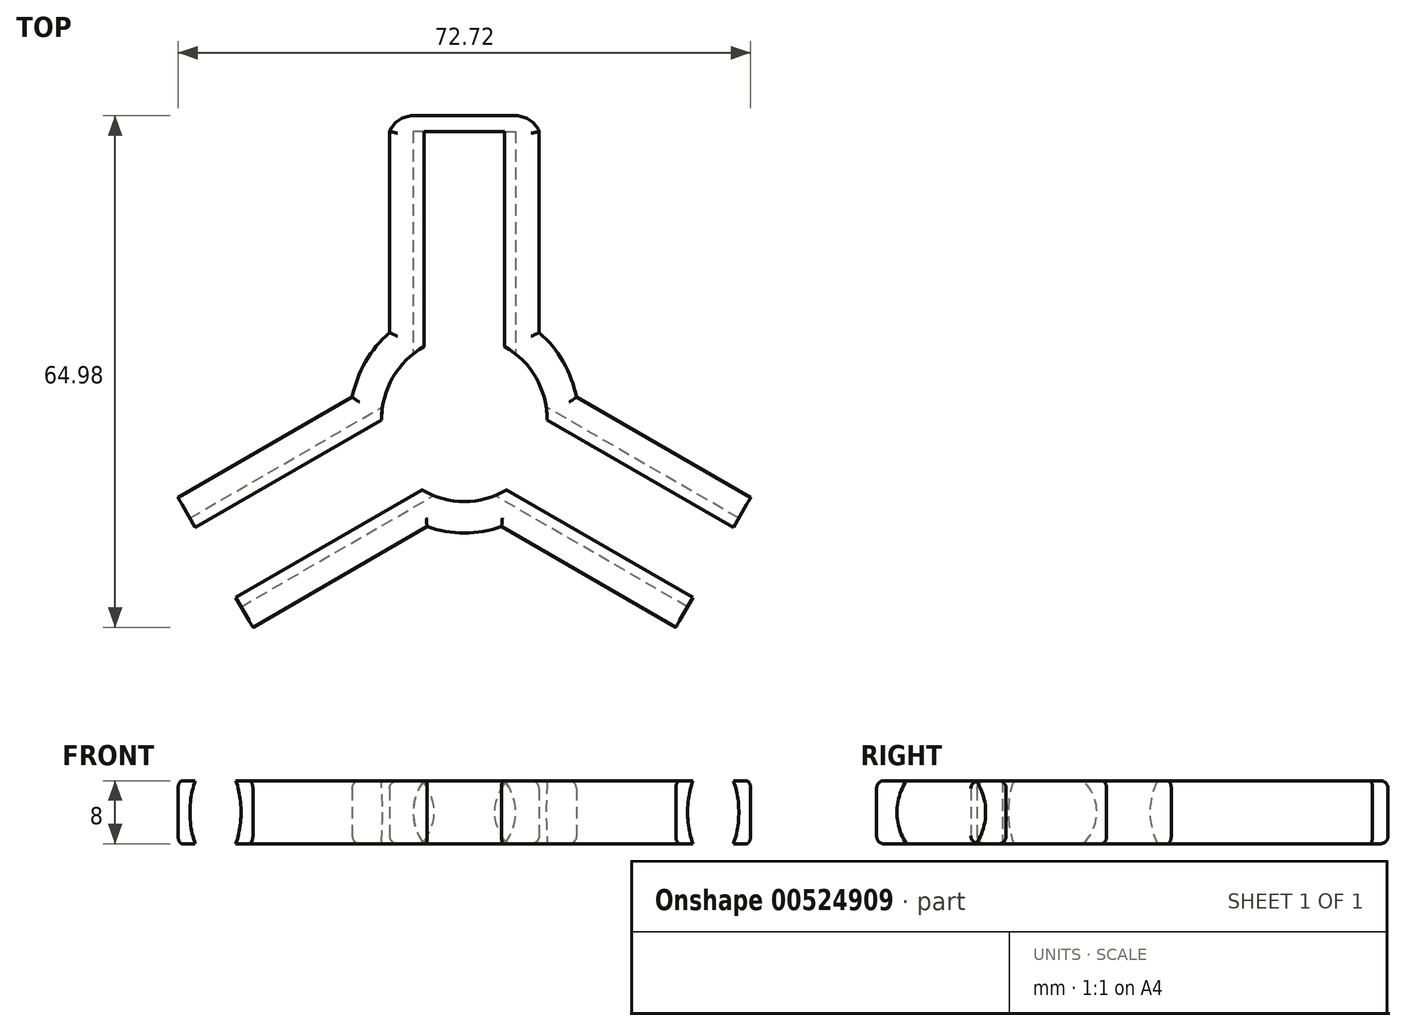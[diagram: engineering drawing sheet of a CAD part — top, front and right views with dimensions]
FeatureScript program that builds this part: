
annotation { "Feature Type Name" : "Feature", "Feature Type Description" : "" }
export const myFeature = defineFeature(function(context is Context, id is Id, definition is map)
    precondition{}
    {
        {
            var Q0;
            Q0=qCreatedBy(makeId("Top.planeOp"),FACE);
            var sketch = newSketch(context, id + "F0", { "sketchPlane" : qUnion([Q0])});
            skCircle(sketch, "E0", {"center": v(0, 0) * mm, "radius": 10.5 * mm});
            skCircle(sketch, "E1.0", {"center": v(0, 0) * mm, "radius": 14.5 * mm});
            skLineSegment(sketch, "E2", {"start": v(0, 36.5) * mm, "end": v(0, 10.5) * mm});
            skLineSegment(sketch, "E3", {"start": v(0, 36.5) * mm, "end": v(6.5, 36.5) * mm});
            skLineSegment(sketch, "E4.MirrorCS", {"start": v(0, 36.5) * mm, "end": v(-6.5, 36.5) * mm});
            skLineSegment(sketch, "E5.0", {"start": v(0, 38.5) * mm, "end": v(6.5, 38.5) * mm});
            skLineSegment(sketch, "E5.1", {"start": v(0, 38.5) * mm, "end": v(-6.5, 38.5) * mm});
            skLineSegment(sketch, "E6", {"start": v(-6.5, 36.5) * mm, "end": v(-6.5, 8.25) * mm});
            skLineSegment(sketch, "E7.0", {"start": v(-9.5, 36.5) * mm, "end": v(-9.5, 10.95) * mm});
            skArc(sketch, "E8", {"start": v(-6.5, 38.5) * mm, "mid": v(-8.3, 37.95) * mm, "end": v(-9.5, 36.5) * mm});
            skLineSegment(sketch, "E9.MirrorCS", {"start": v(6.5, 36.5) * mm, "end": v(6.5, 8.25) * mm});
            skLineSegment(sketch, "E10.MirrorCS", {"start": v(9.5, 36.5) * mm, "end": v(9.5, 10.95) * mm});
            skArc(sketch, "E11.MirrorCS", {"start": v(6.5, 38.5) * mm, "mid": v(8.3, 37.95) * mm, "end": v(9.5, 36.5) * mm});
            skPoint(sketch, "E12.orphan", {"position": v(9.5, 8.25) * mm});
            skPoint(sketch, "E13.orphan", {"position": v(-9.5, 8.25) * mm});
            skLineSegment(sketch, "E14.1.0", {"start": v(-34.86, -12.62) * mm, "end": v(-10.4, 1.5) * mm});
            skLineSegment(sketch, "E14.1.1", {"start": v(-36.36, -10.02) * mm, "end": v(-14.24, 2.75) * mm});
            skArc(sketch, "E14.1.2", {"start": v(-36.6, -13.62) * mm, "mid": v(-37.02, -11.79) * mm, "end": v(-36.36, -10.02) * mm});
            skLineSegment(sketch, "E14.1.3", {"start": v(-33.34, -19.25) * mm, "end": v(-36.6, -13.62) * mm});
            skLineSegment(sketch, "E14.1.4", {"start": v(-31.6, -18.25) * mm, "end": v(-34.86, -12.62) * mm});
            skLineSegment(sketch, "E14.1.5", {"start": v(-31.6, -18.25) * mm, "end": v(-28.36, -23.88) * mm});
            skLineSegment(sketch, "E14.1.6", {"start": v(-33.34, -19.25) * mm, "end": v(-30.1, -24.88) * mm});
            skLineSegment(sketch, "E14.1.7", {"start": v(-31.6, -18.25) * mm, "end": v(-9.1, -5.25) * mm});
            skLineSegment(sketch, "E14.1.8", {"start": v(-28.36, -23.88) * mm, "end": v(-3.9, -9.75) * mm});
            skLineSegment(sketch, "E14.1.9", {"start": v(-26.86, -26.48) * mm, "end": v(-4.74, -13.7) * mm});
            skArc(sketch, "E14.1.10", {"start": v(-30.1, -24.88) * mm, "mid": v(-28.72, -26.17) * mm, "end": v(-26.86, -26.48) * mm});
            skLineSegment(sketch, "E14.2.0", {"start": v(28.36, -23.88) * mm, "end": v(3.9, -9.75) * mm});
            skLineSegment(sketch, "E14.2.1", {"start": v(26.86, -26.48) * mm, "end": v(4.74, -13.7) * mm});
            skArc(sketch, "E14.2.2", {"start": v(30.1, -24.88) * mm, "mid": v(28.72, -26.17) * mm, "end": v(26.86, -26.48) * mm});
            skLineSegment(sketch, "E14.2.3", {"start": v(33.34, -19.25) * mm, "end": v(30.1, -24.88) * mm});
            skLineSegment(sketch, "E14.2.4", {"start": v(31.6, -18.25) * mm, "end": v(28.36, -23.88) * mm});
            skLineSegment(sketch, "E14.2.5", {"start": v(31.6, -18.25) * mm, "end": v(34.86, -12.62) * mm});
            skLineSegment(sketch, "E14.2.6", {"start": v(33.34, -19.25) * mm, "end": v(36.6, -13.62) * mm});
            skLineSegment(sketch, "E14.2.7", {"start": v(31.6, -18.25) * mm, "end": v(9.1, -5.25) * mm});
            skLineSegment(sketch, "E14.2.8", {"start": v(34.86, -12.62) * mm, "end": v(10.4, 1.5) * mm});
            skLineSegment(sketch, "E14.2.9", {"start": v(36.36, -10.02) * mm, "end": v(14.24, 2.75) * mm});
            skArc(sketch, "E14.2.10", {"start": v(36.6, -13.62) * mm, "mid": v(37.02, -11.79) * mm, "end": v(36.36, -10.02) * mm});
            skLineSegment(sketch, "E15", {"start": v(0, 10.5) * mm, "end": v(0, 5.05) * mm});
            skLineSegment(sketch, "E16.1.0", {"start": v(-9.1, -5.25) * mm, "end": v(-4.37, -2.52) * mm});
            skLineSegment(sketch, "E16.2.0", {"start": v(9.1, -5.25) * mm, "end": v(4.37, -2.52) * mm});
            skLineSegment(sketch, "E17", {"start": v(6.5, 36.5) * mm, "end": v(13.9, 36.5) * mm});
            skLineSegment(sketch, "E18", {"start": v(-6.5, 36.5) * mm, "end": v(-15.3, 36.5) * mm});
            skLineSegment(sketch, "E19.1.0", {"start": v(-28.36, -23.88) * mm, "end": v(-23.96, -31.5) * mm});
            skLineSegment(sketch, "E19.1.1", {"start": v(-34.86, -12.62) * mm, "end": v(-38.56, -6.21) * mm});
            skLineSegment(sketch, "E19.2.0", {"start": v(34.86, -12.62) * mm, "end": v(39.26, -5) * mm});
            skLineSegment(sketch, "E19.2.1", {"start": v(28.36, -23.88) * mm, "end": v(24.66, -30.29) * mm});
            skSolve(sketch);
        }
        {
            var Q0;
            {var subQ0=sQuery(id+"F0.wireOp",EDGE,"E7.0");Q0=makeQuery(id+"F0.imprint","IMPRINT",FACE,{"disambiguationData":[TD([[makeQuery(id+"F0.imprint","IMPRINT",EDGE,{"derivedFrom":subQ0}),1.0]])]});}
            var Q1;
            {var subQ0=sQuery(id+"F0.wireOp",EDGE,"E10.MirrorCS");Q1=makeQuery(id+"F0.imprint","IMPRINT",FACE,{"disambiguationData":[TD([[makeQuery(id+"F0.imprint","IMPRINT",EDGE,{"derivedFrom":subQ0}),-1.0]])]});}
            var Q2;
            {var subQ0=sQuery(id+"F0.wireOp",EDGE,"E2");var subQ1=sQuery(id+"F0.wireOp",EDGE,"E0");var subQ2=makeQuery(id+"F0.imprint","INTERSECT",VERTEX,{"derivedFrom":[subQ1,subQ0]});Q2=makeQuery(id+"F0.imprint","IMPRINT",FACE,{"disambiguationData":[TD([[makeQuery(id+"F0.imprint","IMPRINT",EDGE,{"disambiguationData":[TD([[subQ2,1.0]])],"derivedFrom":subQ1}),-1.0]])]});}
            var Q3;
            {var subQ5=sQuery(id+"F0.wireOp",EDGE,"E9.MirrorCS");var subQ7=sQuery(id+"F0.wireOp",EDGE,"E0");var subQ8=makeQuery(id+"F0.imprint","INTERSECT",VERTEX,{"derivedFrom":[subQ7,subQ5]});Q3=makeQuery(id+"F0.imprint","IMPRINT",FACE,{"disambiguationData":[TD([[makeQuery(id+"F0.imprint","IMPRINT",EDGE,{"disambiguationData":[TD([[subQ8,1.0]])],"derivedFrom":subQ7}),-1.0]])]});}
            var Q4;
            {var subQ0=sQuery(id+"F0.wireOp",EDGE,"E2");var subQ1=sQuery(id+"F0.wireOp",EDGE,"E0");var subQ2=makeQuery(id+"F0.imprint","INTERSECT",VERTEX,{"derivedFrom":[subQ1,subQ0]});Q4=makeQuery(id+"F0.imprint","IMPRINT",FACE,{"disambiguationData":[TD([[makeQuery(id+"F0.imprint","IMPRINT",EDGE,{"disambiguationData":[TD([[subQ2,-1.0]])],"derivedFrom":subQ1}),-1.0]])]});}
            var Q5;
            {var subQ5=sQuery(id+"F0.wireOp",EDGE,"E6");var subQ6=sQuery(id+"F0.wireOp",EDGE,"E0");var subQ7=makeQuery(id+"F0.imprint","INTERSECT",VERTEX,{"derivedFrom":[subQ6,subQ5]});Q5=makeQuery(id+"F0.imprint","IMPRINT",FACE,{"disambiguationData":[TD([[makeQuery(id+"F0.imprint","IMPRINT",EDGE,{"disambiguationData":[TD([[subQ7,-1.0]])],"derivedFrom":subQ6}),-1.0]])]});}
            var Q6;
            {var subQ0=sQuery(id+"F0.wireOp",EDGE,"E14.1.1");Q6=makeQuery(id+"F0.imprint","IMPRINT",FACE,{"disambiguationData":[TD([[makeQuery(id+"F0.imprint","IMPRINT",EDGE,{"derivedFrom":subQ0}),-1.0]])]});}
            var Q7;
            {var subQ0=sQuery(id+"F0.wireOp",EDGE,"E14.1.0");var subQ1=sQuery(id+"F0.wireOp",EDGE,"E0");var subQ2=makeQuery(id+"F0.imprint","INTERSECT",VERTEX,{"derivedFrom":[subQ1,subQ0]});Q7=makeQuery(id+"F0.imprint","IMPRINT",FACE,{"disambiguationData":[TD([[makeQuery(id+"F0.imprint","IMPRINT",EDGE,{"disambiguationData":[TD([[subQ2,-1.0]])],"derivedFrom":subQ1}),-1.0]])]});}
            var Q8;
            {var subQ0=sQuery(id+"F0.wireOp",EDGE,"E14.1.7");var subQ1=sQuery(id+"F0.wireOp",EDGE,"E0");var subQ2=makeQuery(id+"F0.imprint","INTERSECT",VERTEX,{"derivedFrom":[subQ1,subQ0]});Q8=makeQuery(id+"F0.imprint","IMPRINT",FACE,{"disambiguationData":[TD([[makeQuery(id+"F0.imprint","IMPRINT",EDGE,{"disambiguationData":[TD([[subQ2,-1.0]])],"derivedFrom":subQ1}),-1.0]])]});}
            var Q9;
            {var subQ0=sQuery(id+"F0.wireOp",EDGE,"E14.1.9");Q9=makeQuery(id+"F0.imprint","IMPRINT",FACE,{"disambiguationData":[TD([[makeQuery(id+"F0.imprint","IMPRINT",EDGE,{"derivedFrom":subQ0}),1.0]])]});}
            var Q10;
            {var subQ4=sQuery(id+"F0.wireOp",EDGE,"E0");var subQ7=sQuery(id+"F0.wireOp",EDGE,"E14.1.8");var subQ9=makeQuery(id+"F0.imprint","INTERSECT",VERTEX,{"derivedFrom":[subQ4,subQ7]});Q10=makeQuery(id+"F0.imprint","IMPRINT",FACE,{"disambiguationData":[TD([[makeQuery(id+"F0.imprint","IMPRINT",EDGE,{"disambiguationData":[TD([[subQ9,-1.0]])],"derivedFrom":subQ4}),-1.0]])]});}
            var Q11;
            {var subQ0=sQuery(id+"F0.wireOp",EDGE,"E14.2.1");Q11=makeQuery(id+"F0.imprint","IMPRINT",FACE,{"disambiguationData":[TD([[makeQuery(id+"F0.imprint","IMPRINT",EDGE,{"derivedFrom":subQ0}),-1.0]])]});}
            var Q12;
            {var subQ0=sQuery(id+"F0.wireOp",EDGE,"E14.2.0");var subQ1=sQuery(id+"F0.wireOp",EDGE,"E0");var subQ2=makeQuery(id+"F0.imprint","INTERSECT",VERTEX,{"derivedFrom":[subQ1,subQ0]});Q12=makeQuery(id+"F0.imprint","IMPRINT",FACE,{"disambiguationData":[TD([[makeQuery(id+"F0.imprint","IMPRINT",EDGE,{"disambiguationData":[TD([[subQ2,-1.0]])],"derivedFrom":subQ1}),-1.0]])]});}
            var Q13;
            {var subQ0=sQuery(id+"F0.wireOp",EDGE,"E14.2.7");var subQ1=sQuery(id+"F0.wireOp",EDGE,"E0");var subQ2=makeQuery(id+"F0.imprint","INTERSECT",VERTEX,{"derivedFrom":[subQ1,subQ0]});Q13=makeQuery(id+"F0.imprint","IMPRINT",FACE,{"disambiguationData":[TD([[makeQuery(id+"F0.imprint","IMPRINT",EDGE,{"disambiguationData":[TD([[subQ2,-1.0]])],"derivedFrom":subQ1}),-1.0]])]});}
            var Q14;
            {var subQ0=sQuery(id+"F0.wireOp",EDGE,"E14.2.9");Q14=makeQuery(id+"F0.imprint","IMPRINT",FACE,{"disambiguationData":[TD([[makeQuery(id+"F0.imprint","IMPRINT",EDGE,{"derivedFrom":subQ0}),1.0]])]});}
            var Q15;
            {var subQ5=sQuery(id+"F0.wireOp",EDGE,"E3");Q15=makeQuery(id+"F0.imprint","IMPRINT",FACE,{"disambiguationData":[TD([[makeQuery(id+"F0.imprint","IMPRINT",EDGE,{"derivedFrom":subQ5}),-1.0]])]});}
            var Q16;
            {var subQ5=sQuery(id+"F0.wireOp",EDGE,"E4.MirrorCS");Q16=makeQuery(id+"F0.imprint","IMPRINT",FACE,{"disambiguationData":[TD([[makeQuery(id+"F0.imprint","IMPRINT",EDGE,{"derivedFrom":subQ5}),1.0]])]});}
            var Q17;
            {var subQ5=sQuery(id+"F0.wireOp",EDGE,"E14.1.4");Q17=makeQuery(id+"F0.imprint","IMPRINT",FACE,{"disambiguationData":[TD([[makeQuery(id+"F0.imprint","IMPRINT",EDGE,{"derivedFrom":subQ5}),-1.0]])]});}
            var Q18;
            {var subQ5=sQuery(id+"F0.wireOp",EDGE,"E14.1.5");Q18=makeQuery(id+"F0.imprint","IMPRINT",FACE,{"disambiguationData":[TD([[makeQuery(id+"F0.imprint","IMPRINT",EDGE,{"derivedFrom":subQ5}),1.0]])]});}
            var Q19;
            {var subQ5=sQuery(id+"F0.wireOp",EDGE,"E14.2.4");Q19=makeQuery(id+"F0.imprint","IMPRINT",FACE,{"disambiguationData":[TD([[makeQuery(id+"F0.imprint","IMPRINT",EDGE,{"derivedFrom":subQ5}),-1.0]])]});}
            var Q20;
            {var subQ5=sQuery(id+"F0.wireOp",EDGE,"E14.2.5");Q20=makeQuery(id+"F0.imprint","IMPRINT",FACE,{"disambiguationData":[TD([[makeQuery(id+"F0.imprint","IMPRINT",EDGE,{"derivedFrom":subQ5}),1.0]])]});}
            extrude(context, id + "F1", {"entities" : qUnion([Q0, Q1, Q2, Q3, Q4, Q5, Q6, Q7, Q8, Q9, Q10, Q11, Q12, Q13, Q14, Q15, Q16, Q17, Q18, Q19, Q20]), "endBound" : BoundingType.SYMMETRIC, "depth" : 8 * mm, "offsetDistance" : 25 * mm});
        }
        {
            var Q0;
            Q0=makeQuery(id+"F1.opExtrude","SWEPT_FACE",FACE,{"disambiguationData":[OSD([sQuery(id+"F0.wireOp",EDGE,"E18")])]});
            cPlane(context, id + "F2", {"entities" : qUnion([Q0]), "cplaneType" : CPlaneType.OFFSET, "offset" : 0 * mm, "width" : 150 * mm, "height" : 150 * mm});
        }
        {
            var Q0;
            Q0=qCreatedBy(id+"F2.planeOp",FACE);
            var sketch = newSketch(context, id + "F3", { "sketchPlane" : qUnion([Q0])});
            skCircle(sketch, "E20", {"center": v(0, 0) * mm, "radius": 6.5 * mm});
            skSolve(sketch);
        }
        {
            var Q0;
            Q0=makeQuery(id+"F3.imprint","IMPRINT",FACE,{"disambiguationData":[TD([[makeQuery(id+"F3.imprint","IMPRINT",EDGE,{"derivedFrom":sQuery(id+"F3.wireOp",EDGE,"E20")}),1.0]])]});
            var Q1;
            Q1=sQuery(id+"F0.wireOp",EDGE,"E2");
            var Q2;
            Q2=sQuery(id+"F0.wireOp",EDGE,"E15");
            sweep(context, id + "F4", {"operationType" : NewBodyOperationType.REMOVE, "profiles" : qUnion([Q0]), "path" : qUnion([Q1, Q2])});
        }
        {
            var Q0;
            Q0=makeQuery(id+"F1.opExtrude","SWEPT_FACE",FACE,{"disambiguationData":[OSD([sQuery(id+"F0.wireOp",EDGE,"E14.1.4"),sQuery(id+"F0.wireOp",EDGE,"E14.1.5"),sQuery(id+"F0.wireOp",EDGE,"E19.1.0"),sQuery(id+"F0.wireOp",EDGE,"E19.1.1")])]});
            cPlane(context, id + "F5", {"entities" : qUnion([Q0]), "cplaneType" : CPlaneType.OFFSET, "offset" : 0 * mm, "width" : 150 * mm, "height" : 150 * mm});
        }
        {
            var Q0;
            Q0=qCreatedBy(id+"F5.planeOp",FACE);
            var sketch = newSketch(context, id + "F6", { "sketchPlane" : qUnion([Q0])});
            skCircle(sketch, "E21", {"center": v(0, 0) * mm, "radius": 6.5 * mm});
            skSolve(sketch);
        }
        {
            var Q0;
            Q0=makeQuery(id+"F6.imprint","IMPRINT",FACE,{"disambiguationData":[TD([[makeQuery(id+"F6.imprint","IMPRINT",EDGE,{"derivedFrom":sQuery(id+"F6.wireOp",EDGE,"E21")}),1.0]])]});
            var Q1;
            Q1=sQuery(id+"F0.wireOp",EDGE,"E14.1.7");
            var Q2;
            Q2=sQuery(id+"F0.wireOp",EDGE,"E16.1.0");
            sweep(context, id + "F7", {"operationType" : NewBodyOperationType.REMOVE, "profiles" : qUnion([Q0]), "path" : qUnion([Q1, Q2])});
        }
        {
            var Q0;
            Q0=makeQuery(id+"F1.opExtrude","SWEPT_FACE",FACE,{"disambiguationData":[OSD([sQuery(id+"F0.wireOp",EDGE,"E14.2.4"),sQuery(id+"F0.wireOp",EDGE,"E14.2.5"),sQuery(id+"F0.wireOp",EDGE,"E19.2.0"),sQuery(id+"F0.wireOp",EDGE,"E19.2.1")])]});
            cPlane(context, id + "F8", {"entities" : qUnion([Q0]), "cplaneType" : CPlaneType.OFFSET, "offset" : 0 * mm, "width" : 150 * mm, "height" : 150 * mm});
        }
        {
            var Q0;
            Q0=qCreatedBy(id+"F8.planeOp",FACE);
            var sketch = newSketch(context, id + "F9", { "sketchPlane" : qUnion([Q0])});
            skCircle(sketch, "E22", {"center": v(0, 0) * mm, "radius": 6.5 * mm});
            skSolve(sketch);
        }
        {
            var Q0;
            Q0=makeQuery(id+"F9.imprint","IMPRINT",FACE,{"disambiguationData":[TD([[makeQuery(id+"F9.imprint","IMPRINT",EDGE,{"derivedFrom":sQuery(id+"F9.wireOp",EDGE,"E22")}),1.0]])]});
            var Q1;
            Q1=sQuery(id+"F0.wireOp",EDGE,"E14.2.7");
            var Q2;
            Q2=sQuery(id+"F0.wireOp",EDGE,"E16.2.0");
            sweep(context, id + "F10", {"operationType" : NewBodyOperationType.REMOVE, "profiles" : qUnion([Q0]), "path" : qUnion([Q1, Q2])});
        }
        {
            var Q0;
            {var subQ1=sQuery(id+"F0.wireOp",EDGE,"E3");Q0=makeQuery(id+"F0.imprint","IMPRINT",FACE,{"disambiguationData":[TD([[makeQuery(id+"F0.imprint","IMPRINT",EDGE,{"derivedFrom":subQ1}),1.0]])]});}
            var Q1;
            {var subQ2=sQuery(id+"F0.wireOp",EDGE,"E14.1.2");Q1=makeQuery(id+"F0.imprint","IMPRINT",FACE,{"disambiguationData":[TD([[makeQuery(id+"F0.imprint","IMPRINT",EDGE,{"derivedFrom":subQ2}),-1.0]])]});}
            var Q2;
            {var subQ2=sQuery(id+"F0.wireOp",EDGE,"E14.2.2");Q2=makeQuery(id+"F0.imprint","IMPRINT",FACE,{"disambiguationData":[TD([[makeQuery(id+"F0.imprint","IMPRINT",EDGE,{"derivedFrom":subQ2}),-1.0]])]});}
            extrude(context, id + "F11", {"entities" : qUnion([Q0, Q1, Q2]), "operationType" : NewBodyOperationType.ADD, "endBound" : BoundingType.SYMMETRIC, "depth" : 8 * mm, "offsetDistance" : 25 * mm});
        }
        {
            var Q0;
            Q0=makeQuery(id+"F1.opExtrude","CAP_EDGE",EDGE,{"disambiguationData":[OSD([sQuery(id+"F0.wireOp",EDGE,"E7.0")])],"isStart":true});
            var Q1;
            Q1=makeQuery(id+"F1.opExtrude","CAP_EDGE",EDGE,{"disambiguationData":[OSD([sQuery(id+"F0.wireOp",EDGE,"E10.MirrorCS")])],"isStart":true});
            var Q2;
            Q2=makeQuery(id+"F11.opExtrude","CAP_EDGE",EDGE,{"disambiguationData":[OSD([sQuery(id+"F0.wireOp",EDGE,"E5.0"),sQuery(id+"F0.wireOp",EDGE,"E5.1")])],"isStart":true});
            var Q3;
            {var subQ0=sQuery(id+"F0.wireOp",EDGE,"E1.0");Q3=makeQuery(id+"F1.opExtrude","CAP_EDGE",EDGE,{"disambiguationData":[OSD([subQ0]),TDD([makeQuery(id+"F0.imprint","IMPRINT",EDGE,{"disambiguationData":[TD([[makeQuery(id+"F0.imprint","INTERSECT",VERTEX,{"derivedFrom":[subQ0,sQuery(id+"F0.wireOp",EDGE,"E7.0")]}),-1.0]])],"derivedFrom":subQ0})])],"isStart":true});}
            var Q4;
            Q4=makeQuery(id+"F1.opExtrude","CAP_EDGE",EDGE,{"disambiguationData":[OSD([sQuery(id+"F0.wireOp",EDGE,"E14.1.1")])],"isStart":true});
            var Q5;
            Q5=makeQuery(id+"F11.opExtrude","CAP_EDGE",EDGE,{"disambiguationData":[OSD([sQuery(id+"F0.wireOp",EDGE,"E14.1.3"),sQuery(id+"F0.wireOp",EDGE,"E14.1.6")])],"isStart":true});
            var Q6;
            Q6=makeQuery(id+"F1.opExtrude","CAP_EDGE",EDGE,{"disambiguationData":[OSD([sQuery(id+"F0.wireOp",EDGE,"E14.1.9")])],"isStart":true});
            var Q7;
            {var subQ0=sQuery(id+"F0.wireOp",EDGE,"E1.0");Q7=makeQuery(id+"F1.opExtrude","CAP_EDGE",EDGE,{"disambiguationData":[OSD([subQ0]),TDD([makeQuery(id+"F0.imprint","IMPRINT",EDGE,{"disambiguationData":[TD([[makeQuery(id+"F0.imprint","INTERSECT",VERTEX,{"derivedFrom":[subQ0,sQuery(id+"F0.wireOp",EDGE,"E14.1.9")]}),-1.0]])],"derivedFrom":subQ0})])],"isStart":true});}
            var Q8;
            Q8=makeQuery(id+"F1.opExtrude","CAP_EDGE",EDGE,{"disambiguationData":[OSD([sQuery(id+"F0.wireOp",EDGE,"E14.2.1")])],"isStart":true});
            var Q9;
            Q9=makeQuery(id+"F11.opExtrude","CAP_EDGE",EDGE,{"disambiguationData":[OSD([sQuery(id+"F0.wireOp",EDGE,"E14.2.3"),sQuery(id+"F0.wireOp",EDGE,"E14.2.6")])],"isStart":true});
            var Q10;
            Q10=makeQuery(id+"F1.opExtrude","CAP_EDGE",EDGE,{"disambiguationData":[OSD([sQuery(id+"F0.wireOp",EDGE,"E14.2.9")])],"isStart":true});
            var Q11;
            {var subQ0=sQuery(id+"F0.wireOp",EDGE,"E1.0");Q11=makeQuery(id+"F1.opExtrude","CAP_EDGE",EDGE,{"disambiguationData":[OSD([subQ0]),TDD([makeQuery(id+"F0.imprint","IMPRINT",EDGE,{"disambiguationData":[TD([[makeQuery(id+"F0.imprint","INTERSECT",VERTEX,{"derivedFrom":[subQ0,sQuery(id+"F0.wireOp",EDGE,"E10.MirrorCS")]}),1.0]])],"derivedFrom":subQ0})])],"isStart":true});}
            var Q12;
            Q12=makeQuery(id+"F11.opExtrude","CAP_EDGE",EDGE,{"disambiguationData":[OSD([sQuery(id+"F0.wireOp",EDGE,"E5.0"),sQuery(id+"F0.wireOp",EDGE,"E5.1")])],"isStart":false});
            var Q13;
            Q13=makeQuery(id+"F1.opExtrude","CAP_EDGE",EDGE,{"disambiguationData":[OSD([sQuery(id+"F0.wireOp",EDGE,"E10.MirrorCS")])],"isStart":false});
            var Q14;
            {var subQ0=sQuery(id+"F0.wireOp",EDGE,"E1.0");Q14=makeQuery(id+"F1.opExtrude","CAP_EDGE",EDGE,{"disambiguationData":[OSD([subQ0]),TDD([makeQuery(id+"F0.imprint","IMPRINT",EDGE,{"disambiguationData":[TD([[makeQuery(id+"F0.imprint","INTERSECT",VERTEX,{"derivedFrom":[subQ0,sQuery(id+"F0.wireOp",EDGE,"E10.MirrorCS")]}),1.0]])],"derivedFrom":subQ0})])],"isStart":false});}
            var Q15;
            Q15=makeQuery(id+"F1.opExtrude","CAP_EDGE",EDGE,{"disambiguationData":[OSD([sQuery(id+"F0.wireOp",EDGE,"E14.2.9")])],"isStart":false});
            var Q16;
            Q16=makeQuery(id+"F11.opExtrude","CAP_EDGE",EDGE,{"disambiguationData":[OSD([sQuery(id+"F0.wireOp",EDGE,"E14.2.3"),sQuery(id+"F0.wireOp",EDGE,"E14.2.6")])],"isStart":false});
            var Q17;
            Q17=makeQuery(id+"F1.opExtrude","CAP_EDGE",EDGE,{"disambiguationData":[OSD([sQuery(id+"F0.wireOp",EDGE,"E14.2.1")])],"isStart":false});
            var Q18;
            {var subQ0=sQuery(id+"F0.wireOp",EDGE,"E1.0");Q18=makeQuery(id+"F1.opExtrude","CAP_EDGE",EDGE,{"disambiguationData":[OSD([subQ0]),TDD([makeQuery(id+"F0.imprint","IMPRINT",EDGE,{"disambiguationData":[TD([[makeQuery(id+"F0.imprint","INTERSECT",VERTEX,{"derivedFrom":[subQ0,sQuery(id+"F0.wireOp",EDGE,"E14.1.9")]}),-1.0]])],"derivedFrom":subQ0})])],"isStart":false});}
            var Q19;
            Q19=makeQuery(id+"F1.opExtrude","CAP_EDGE",EDGE,{"disambiguationData":[OSD([sQuery(id+"F0.wireOp",EDGE,"E14.1.9")])],"isStart":false});
            var Q20;
            Q20=makeQuery(id+"F11.opExtrude","CAP_EDGE",EDGE,{"disambiguationData":[OSD([sQuery(id+"F0.wireOp",EDGE,"E14.1.3"),sQuery(id+"F0.wireOp",EDGE,"E14.1.6")])],"isStart":false});
            var Q21;
            Q21=makeQuery(id+"F1.opExtrude","CAP_EDGE",EDGE,{"disambiguationData":[OSD([sQuery(id+"F0.wireOp",EDGE,"E14.1.1")])],"isStart":false});
            var Q22;
            {var subQ0=sQuery(id+"F0.wireOp",EDGE,"E1.0");Q22=makeQuery(id+"F1.opExtrude","CAP_EDGE",EDGE,{"disambiguationData":[OSD([subQ0]),TDD([makeQuery(id+"F0.imprint","IMPRINT",EDGE,{"disambiguationData":[TD([[makeQuery(id+"F0.imprint","INTERSECT",VERTEX,{"derivedFrom":[subQ0,sQuery(id+"F0.wireOp",EDGE,"E7.0")]}),-1.0]])],"derivedFrom":subQ0})])],"isStart":false});}
            var Q23;
            Q23=makeQuery(id+"F1.opExtrude","CAP_EDGE",EDGE,{"disambiguationData":[OSD([sQuery(id+"F0.wireOp",EDGE,"E7.0")])],"isStart":false});
            fillet(context, id + "F12", {"entities" : qUnion([Q0, Q1, Q2, Q3, Q4, Q5, Q6, Q7, Q8, Q9, Q10, Q11, Q12, Q13, Q14, Q15, Q16, Q17, Q18, Q19, Q20, Q21, Q22, Q23]), "radius" : 1 * mm, "tangentPropagation" : true, "allowEdgeOverflow" : false});
        }
    });
